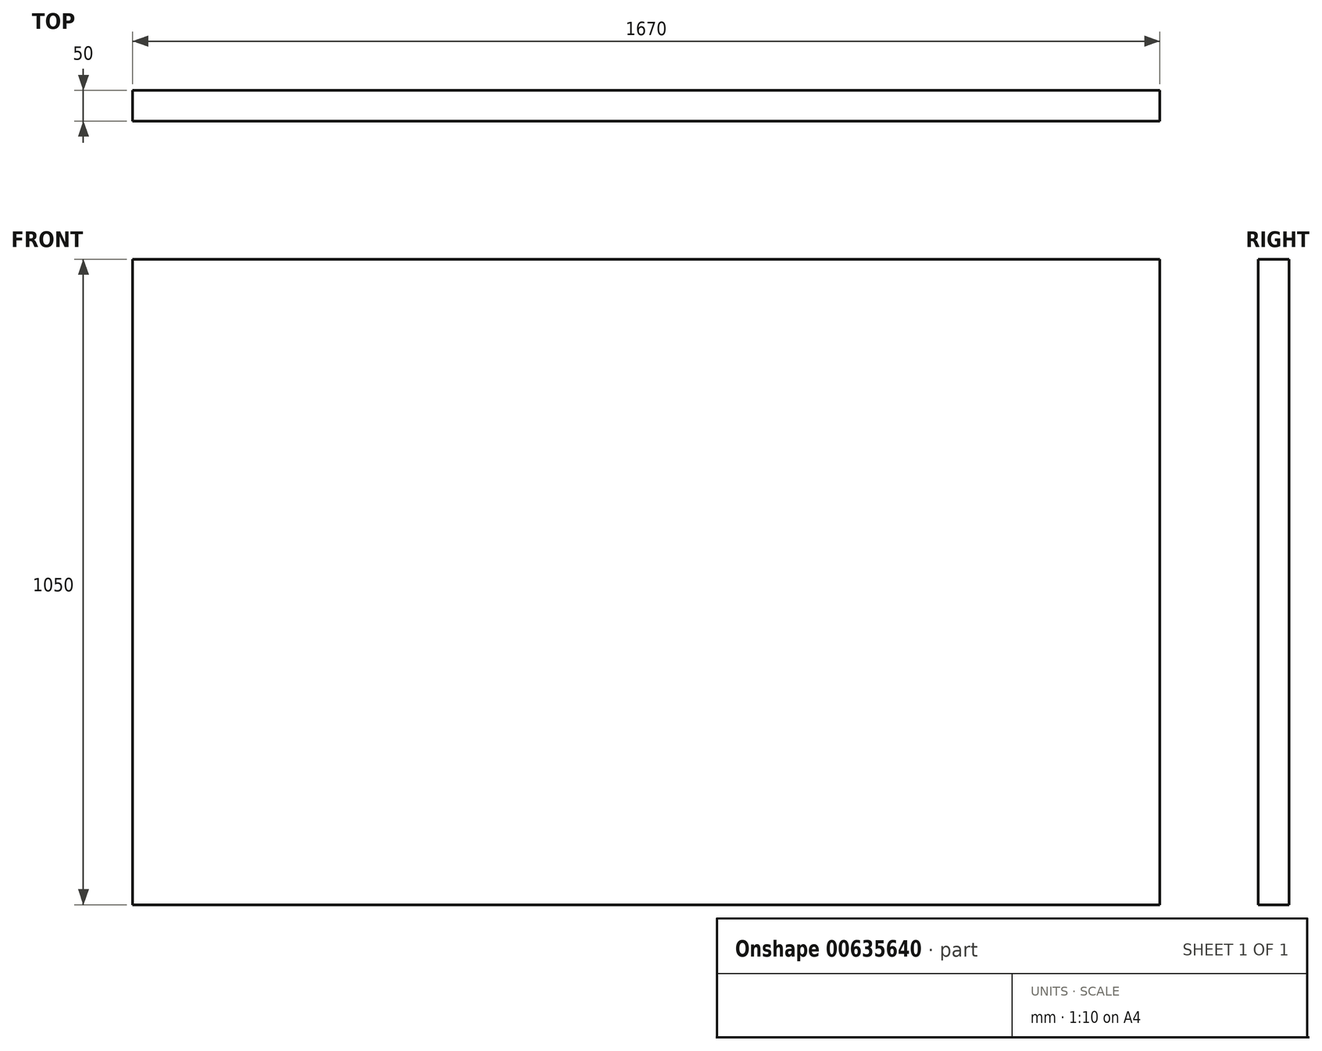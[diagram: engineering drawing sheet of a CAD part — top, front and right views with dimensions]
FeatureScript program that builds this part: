
annotation { "Feature Type Name" : "Feature", "Feature Type Description" : "" }
export const myFeature = defineFeature(function(context is Context, id is Id, definition is map)
    precondition{}
    {
        {
            var Q0;
            Q0=qCreatedBy(makeId("Front.planeOp"),FACE);
            var sketch = newSketch(context, id + "F0", { "sketchPlane" : qUnion([Q0])});
            skLineSegment(sketch, "E0.bottom", {"start": v(835, 525) * mm, "end": v(-835, 525) * mm});
            skLineSegment(sketch, "E0.top", {"start": v(835, -525) * mm, "end": v(-835, -525) * mm});
            skLineSegment(sketch, "E0.left", {"start": v(835, 525) * mm, "end": v(835, -525) * mm});
            skLineSegment(sketch, "E0.right", {"start": v(-835, 525) * mm, "end": v(-835, -525) * mm});
            skPoint(sketch, "E0.middle", {"position": v(0, 0) * mm});
            skSolve(sketch);
        }
        {
            var Q0;
            Q0=makeQuery(id+"F0.imprint","IMPRINT",FACE,{"disambiguationData":[TD([[makeQuery(id+"F0.imprint","IMPRINT",EDGE,{"derivedFrom":sQuery(id+"F0.wireOp",EDGE,"E0.bottom")}),1.0]])]});
            extrude(context, id + "F1", {"entities" : qUnion([Q0]), "depth" : 50 * mm, "offsetDistance" : 25 * mm});
        }
    });
